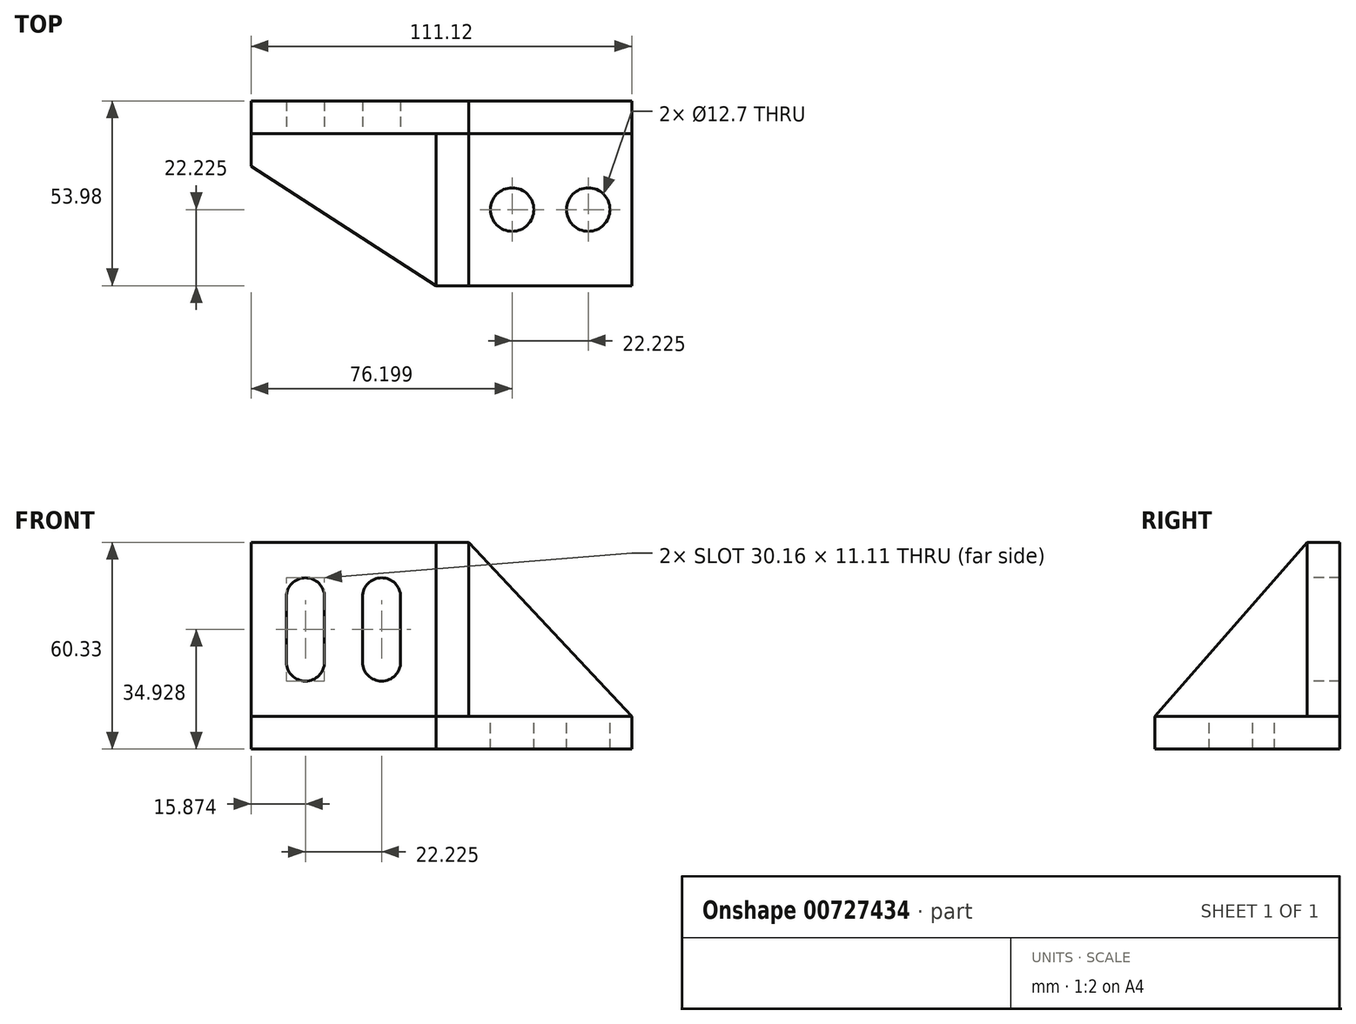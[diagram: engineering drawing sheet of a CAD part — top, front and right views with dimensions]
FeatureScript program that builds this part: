
annotation { "Feature Type Name" : "Feature", "Feature Type Description" : "" }
export const myFeature = defineFeature(function(context is Context, id is Id, definition is map)
    precondition{}
    {
        {
            var Q0;
            Q0=qCreatedBy(makeId("Front.planeOp"),FACE);
            var sketch = newSketch(context, id + "F0", { "sketchPlane" : qUnion([Q0])});
            skLineSegment(sketch, "E0.bottom", {"start": v(-38.84, -20.68) * mm, "end": v(72.28, -20.68) * mm});
            skLineSegment(sketch, "E0.top", {"start": v(-38.84, -30.2) * mm, "end": v(72.28, -30.2) * mm});
            skLineSegment(sketch, "E0.left", {"start": v(-38.84, -20.68) * mm, "end": v(-38.84, -30.2) * mm});
            skLineSegment(sketch, "E0.right", {"start": v(72.28, -20.68) * mm, "end": v(72.28, -30.2) * mm});
            skSolve(sketch);
        }
        {
            var Q0;
            Q0 = qSketchRegion(id + "F0", true);
            extrude(context, id + "F1", {"entities" : qUnion([Q0]), "oppositeDirection" : true, "depth" : 53.97 * mm, "offsetDistance" : 25.4 * mm});
        }
        {
            var Q0;
            Q0=makeQuery(id+"F1.opExtrude","SWEPT_FACE",FACE,{"disambiguationData":[OSD([sQuery(id+"F0.wireOp",EDGE,"E0.bottom")])]});
            var sketch = newSketch(context, id + "F2", { "sketchPlane" : qUnion([Q0])});
            skLineSegment(sketch, "E1", {"start": v(-38.84, 34.92) * mm, "end": v(15.13, 0) * mm});
            skSolve(sketch);
        }
        {
            var Q0;
            {var subQ0=sQuery(id+"F2.wireOp",EDGE,"E1");Q0=makeQuery(id+"F2.imprint","IMPRINT",FACE,{"disambiguationData":[TD([[makeQuery(id+"F2.imprint","IMPRINT",EDGE,{"derivedFrom":subQ0}),-1.0]])]});}
            extrude(context, id + "F3", {"entities" : qUnion([Q0]), "operationType" : NewBodyOperationType.REMOVE, "endBound" : BoundingType.THROUGH_ALL, "oppositeDirection" : true, "depth" : 25.4 * mm, "offsetDistance" : 25.4 * mm});
        }
        {
            var Q0;
            Q0=makeQuery(id+"F1.opExtrude","SWEPT_FACE",FACE,{"disambiguationData":[OSD([sQuery(id+"F0.wireOp",EDGE,"E0.bottom")])]});
            var sketch = newSketch(context, id + "F4", { "sketchPlane" : qUnion([Q0])});
            skLineSegment(sketch, "E2.bottom", {"start": v(72.28, 53.98) * mm, "end": v(-38.84, 53.98) * mm});
            skLineSegment(sketch, "E2.top", {"start": v(72.28, 44.45) * mm, "end": v(-38.84, 44.45) * mm});
            skLineSegment(sketch, "E2.left", {"start": v(72.28, 53.98) * mm, "end": v(72.28, 44.45) * mm});
            skLineSegment(sketch, "E2.right", {"start": v(-38.84, 53.98) * mm, "end": v(-38.84, 44.45) * mm});
            skLineSegment(sketch, "E3.bottom", {"start": v(15.13, 0) * mm, "end": v(24.66, 0) * mm});
            skLineSegment(sketch, "E3.top", {"start": v(15.13, 44.45) * mm, "end": v(24.66, 44.45) * mm});
            skLineSegment(sketch, "E3.left", {"start": v(15.13, 0) * mm, "end": v(15.13, 44.45) * mm});
            skLineSegment(sketch, "E3.right", {"start": v(24.66, 0) * mm, "end": v(24.66, 44.45) * mm});
            skSolve(sketch);
        }
        {
            var Q0;
            Q0=makeQuery(id+"F4.imprint","IMPRINT",FACE,{"disambiguationData":[TD([[makeQuery(id+"F4.imprint","IMPRINT",EDGE,{"derivedFrom":sQuery(id+"F4.wireOp",EDGE,"E3.bottom")}),1.0]])]});
            var Q1;
            Q1=makeQuery(id+"F4.imprint","IMPRINT",FACE,{"disambiguationData":[TD([[makeQuery(id+"F4.imprint","IMPRINT",EDGE,{"derivedFrom":sQuery(id+"F4.wireOp",EDGE,"E2.bottom")}),-1.0]])]});
            extrude(context, id + "F5", {"entities" : qUnion([Q0, Q1]), "operationType" : NewBodyOperationType.ADD, "depth" : 50.8 * mm, "offsetDistance" : 25.4 * mm});
        }
        {
            var Q0;
            Q0=makeQuery(id+"F5.opExtrude","SWEPT_FACE",FACE,{"disambiguationData":[OSD([sQuery(id+"F4.wireOp",EDGE,"E3.right")])]});
            var sketch = newSketch(context, id + "F6", { "sketchPlane" : qUnion([Q0])});
            skLineSegment(sketch, "E4", {"start": v(0, -20.68) * mm, "end": v(44.45, 30.12) * mm});
            skSolve(sketch);
        }
        {
            var Q0;
            Q0=makeQuery(id+"F6.imprint","IMPRINT",FACE,{"disambiguationData":[TD([[makeQuery(id+"F6.imprint","IMPRINT",EDGE,{"derivedFrom":sQuery(id+"F6.wireOp",EDGE,"E4")}),1.0]])]});
            extrude(context, id + "F7", {"entities" : qUnion([Q0]), "operationType" : NewBodyOperationType.REMOVE, "endBound" : BoundingType.THROUGH_ALL, "oppositeDirection" : true, "depth" : 25.4 * mm, "offsetDistance" : 25.4 * mm});
        }
        {
            var Q0;
            {var subQ0=sQuery(id+"F4.wireOp",EDGE,"E2.top");Q0=makeQuery(id+"F5.opExtrude","SWEPT_FACE",FACE,{"disambiguationData":[OSD([subQ0]),TDD([makeQuery(id+"F4.imprint","IMPRINT",EDGE,{"disambiguationData":[TD([[makeQuery(id+"F4.imprint","INTERSECT",VERTEX,{"derivedFrom":[subQ0,sQuery(id+"F4.wireOp",EDGE,"E3.top"),sQuery(id+"F4.wireOp",EDGE,"E3.right")]}),1.0]])],"derivedFrom":subQ0})])]});}
            var sketch = newSketch(context, id + "F8", { "sketchPlane" : qUnion([Q0])});
            skLineSegment(sketch, "E5", {"start": v(24.66, 30.12) * mm, "end": v(72.28, -20.68) * mm});
            skSolve(sketch);
        }
        {
            var Q0;
            Q0=makeQuery(id+"F8.imprint","IMPRINT",FACE,{"disambiguationData":[TD([[makeQuery(id+"F8.imprint","IMPRINT",EDGE,{"derivedFrom":sQuery(id+"F8.wireOp",EDGE,"E5")}),1.0]])]});
            extrude(context, id + "F9", {"entities" : qUnion([Q0]), "operationType" : NewBodyOperationType.REMOVE, "endBound" : BoundingType.THROUGH_ALL, "oppositeDirection" : true, "depth" : 25.4 * mm, "offsetDistance" : 25.4 * mm});
        }
        {
            var Q0;
            {var subQ2=sQuery(id+"F0.wireOp",EDGE,"E0.right");var subQ3=sQuery(id+"F0.wireOp",EDGE,"E0.bottom");Q0=makeQuery(id+"F5.boolean.opBoolean","SPLIT",FACE,{"disambiguationData":[TD([makeQuery(id+"F1.opExtrude","SWEPT_FACE",FACE,{"disambiguationData":[OSD([subQ2])]})])],"derivedFrom":makeQuery(id+"F1.opExtrude","SWEPT_FACE",FACE,{"disambiguationData":[OSD([subQ3])]})});}
            var sketch = newSketch(context, id + "F10", { "sketchPlane" : qUnion([Q0])});
            skCircle(sketch, "E6", {"center": v(59.58, 22.23) * mm, "radius": 6.35 * mm});
            skPoint(sketch, "E6.centerSnap0", {"position": v(72.28, 22.23) * mm});
            skCircle(sketch, "E7", {"center": v(37.36, 22.23) * mm, "radius": 6.35 * mm});
            skSolve(sketch);
        }
        {
            var Q0;
            Q0=makeQuery(id+"F10.imprint","IMPRINT",FACE,{"disambiguationData":[TD([[makeQuery(id+"F10.imprint","IMPRINT",EDGE,{"derivedFrom":sQuery(id+"F10.wireOp",EDGE,"E7")}),1.0]])]});
            var Q1;
            Q1=makeQuery(id+"F10.imprint","IMPRINT",FACE,{"disambiguationData":[TD([[makeQuery(id+"F10.imprint","IMPRINT",EDGE,{"derivedFrom":sQuery(id+"F10.wireOp",EDGE,"E6")}),1.0]])]});
            extrude(context, id + "F11", {"entities" : qUnion([Q0, Q1]), "operationType" : NewBodyOperationType.REMOVE, "endBound" : BoundingType.THROUGH_ALL, "oppositeDirection" : true, "depth" : 25.4 * mm, "offsetDistance" : 25.4 * mm});
        }
        {
            var Q0;
            {var subQ0=sQuery(id+"F4.wireOp",EDGE,"E2.top");Q0=makeQuery(id+"F5.opExtrude","SWEPT_FACE",FACE,{"disambiguationData":[OSD([subQ0]),TDD([makeQuery(id+"F4.imprint","IMPRINT",EDGE,{"disambiguationData":[TD([[makeQuery(id+"F4.imprint","INTERSECT",VERTEX,{"derivedFrom":[subQ0,sQuery(id+"F4.wireOp",EDGE,"E3.top"),sQuery(id+"F4.wireOp",EDGE,"E3.left")]}),-1.0]])],"derivedFrom":subQ0})])]});}
            var sketch = newSketch(context, id + "F12", { "sketchPlane" : qUnion([Q0])});
            skLineSegment(sketch, "E8.bottom", {"start": v(-28.52, 14.24) * mm, "end": v(-17.4, 14.24) * mm});
            skLineSegment(sketch, "E8.top", {"start": v(-28.52, -4.8) * mm, "end": v(-17.4, -4.8) * mm});
            skLineSegment(sketch, "E8.left", {"start": v(-28.52, 14.24) * mm, "end": v(-28.52, -4.8) * mm});
            skLineSegment(sketch, "E8.right", {"start": v(-17.4, 14.24) * mm, "end": v(-17.4, -4.8) * mm});
            skLineSegment(sketch, "E9.bottom", {"start": v(-6.3, 14.24) * mm, "end": v(4.82, 14.24) * mm});
            skLineSegment(sketch, "E9.top", {"start": v(-6.3, -4.8) * mm, "end": v(4.82, -4.8) * mm});
            skLineSegment(sketch, "E9.left", {"start": v(-6.3, 14.24) * mm, "end": v(-6.3, -4.8) * mm});
            skLineSegment(sketch, "E9.right", {"start": v(4.82, 14.24) * mm, "end": v(4.82, -4.8) * mm});
            skLineSegment(sketch, "E10", {"start": v(-22.97, 14.24) * mm, "end": v(-17.4, 14.24) * mm});
            skLineSegment(sketch, "E11", {"start": v(-6.3, 14.24) * mm, "end": v(-0.74, 14.24) * mm});
            skArc(sketch, "E12", {"start": v(-17.4, 14.24) * mm, "mid": v(-22.97, 19.8) * mm, "end": v(-28.52, 14.24) * mm});
            skArc(sketch, "E13", {"start": v(-28.52, -4.8) * mm, "mid": v(-22.97, -10.36) * mm, "end": v(-17.4, -4.8) * mm});
            skArc(sketch, "E14", {"start": v(-6.3, -4.8) * mm, "mid": v(-0.74, -10.36) * mm, "end": v(4.82, -4.8) * mm});
            skArc(sketch, "E15", {"start": v(4.82, 14.24) * mm, "mid": v(-0.74, 19.8) * mm, "end": v(-6.3, 14.24) * mm});
            skSolve(sketch);
        }
        {
            var Q0;
            Q0=makeQuery(id+"F12.imprint","IMPRINT",FACE,{"disambiguationData":[TD([[makeQuery(id+"F12.imprint","IMPRINT",EDGE,{"derivedFrom":sQuery(id+"F12.wireOp",EDGE,"E8.bottom")}),-1.0]])]});
            var Q1;
            Q1=makeQuery(id+"F12.imprint","IMPRINT",FACE,{"disambiguationData":[TD([[makeQuery(id+"F12.imprint","IMPRINT",EDGE,{"derivedFrom":sQuery(id+"F12.wireOp",EDGE,"E8.bottom")}),1.0]])]});
            var Q2;
            Q2=makeQuery(id+"F12.imprint","IMPRINT",FACE,{"disambiguationData":[TD([[makeQuery(id+"F12.imprint","IMPRINT",EDGE,{"derivedFrom":sQuery(id+"F12.wireOp",EDGE,"E9.top")}),-1.0]])]});
            var Q3;
            Q3=makeQuery(id+"F12.imprint","IMPRINT",FACE,{"disambiguationData":[TD([[makeQuery(id+"F12.imprint","IMPRINT",EDGE,{"derivedFrom":sQuery(id+"F12.wireOp",EDGE,"E9.bottom")}),-1.0]])]});
            var Q4;
            Q4=makeQuery(id+"F12.imprint","IMPRINT",FACE,{"disambiguationData":[TD([[makeQuery(id+"F12.imprint","IMPRINT",EDGE,{"derivedFrom":sQuery(id+"F12.wireOp",EDGE,"E9.bottom")}),1.0]])]});
            var Q5;
            Q5=makeQuery(id+"F12.imprint","IMPRINT",FACE,{"disambiguationData":[TD([[makeQuery(id+"F12.imprint","IMPRINT",EDGE,{"derivedFrom":sQuery(id+"F12.wireOp",EDGE,"E8.top")}),-1.0]])]});
            extrude(context, id + "F13", {"entities" : qUnion([Q0, Q1, Q2, Q3, Q4, Q5]), "operationType" : NewBodyOperationType.REMOVE, "endBound" : BoundingType.THROUGH_ALL, "oppositeDirection" : true, "depth" : 25.4 * mm, "offsetDistance" : 25.4 * mm});
        }
    });
